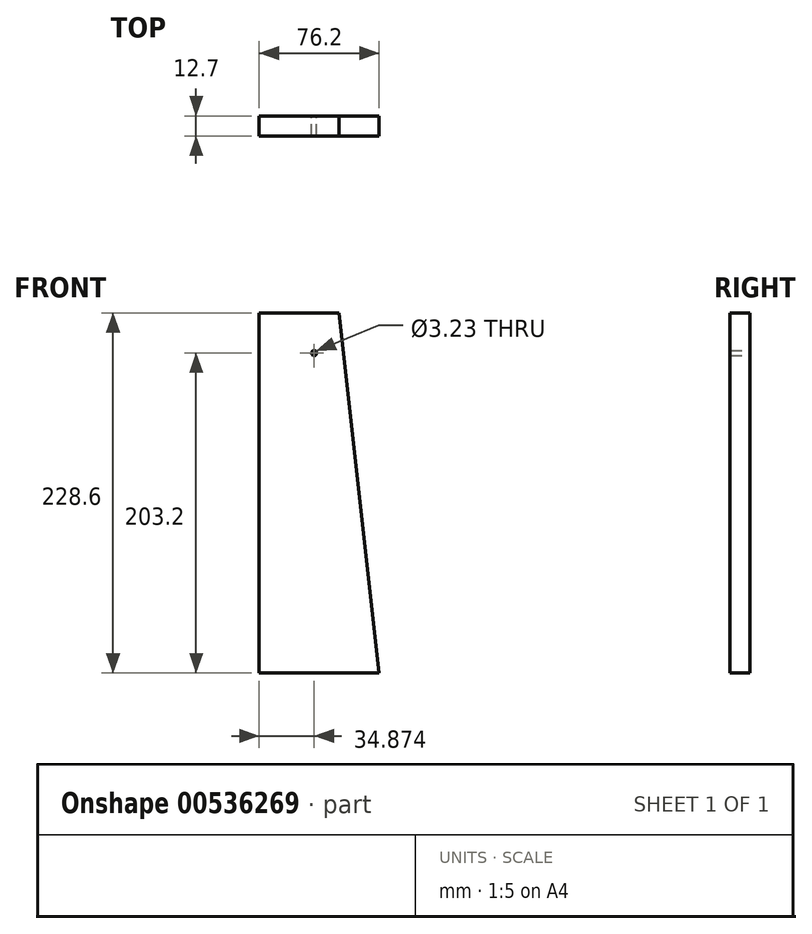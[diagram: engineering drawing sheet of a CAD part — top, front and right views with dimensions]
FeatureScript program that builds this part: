
annotation { "Feature Type Name" : "Feature", "Feature Type Description" : "" }
export const myFeature = defineFeature(function(context is Context, id is Id, definition is map)
    precondition{}
    {
        {
            var Q0;
            Q0=qCreatedBy(makeId("Front.planeOp"),FACE);
            var sketch = newSketch(context, id + "F0", { "sketchPlane" : qUnion([Q0])});
            skLineSegment(sketch, "E0", {"start": v(-76.2, 25.4) * mm, "end": v(-76.2, -203.2) * mm});
            skLineSegment(sketch, "E1", {"start": v(-76.2, -203.2) * mm, "end": v(0, -203.2) * mm});
            skLineSegment(sketch, "E2", {"start": v(-76.2, 25.4) * mm, "end": v(-25.4, 25.4) * mm});
            skLineSegment(sketch, "E3", {"start": v(-25.4, 25.4) * mm, "end": v(0, -203.2) * mm});
            skCircle(sketch, "E4", {"center": v(-41.33, 0) * mm, "radius": 1.61 * mm});
            skSolve(sketch);
        }
        {
            var Q0;
            Q0=makeQuery(id+"F0.imprint","IMPRINT",FACE,{"disambiguationData":[TD([[makeQuery(id+"F0.imprint","IMPRINT",EDGE,{"derivedFrom":sQuery(id+"F0.wireOp",EDGE,"E0")}),1.0]])]});
            extrude(context, id + "F1", {"entities" : qUnion([Q0]), "depth" : 12.7 * mm, "offsetDistance" : 25.4 * mm});
        }
    });
